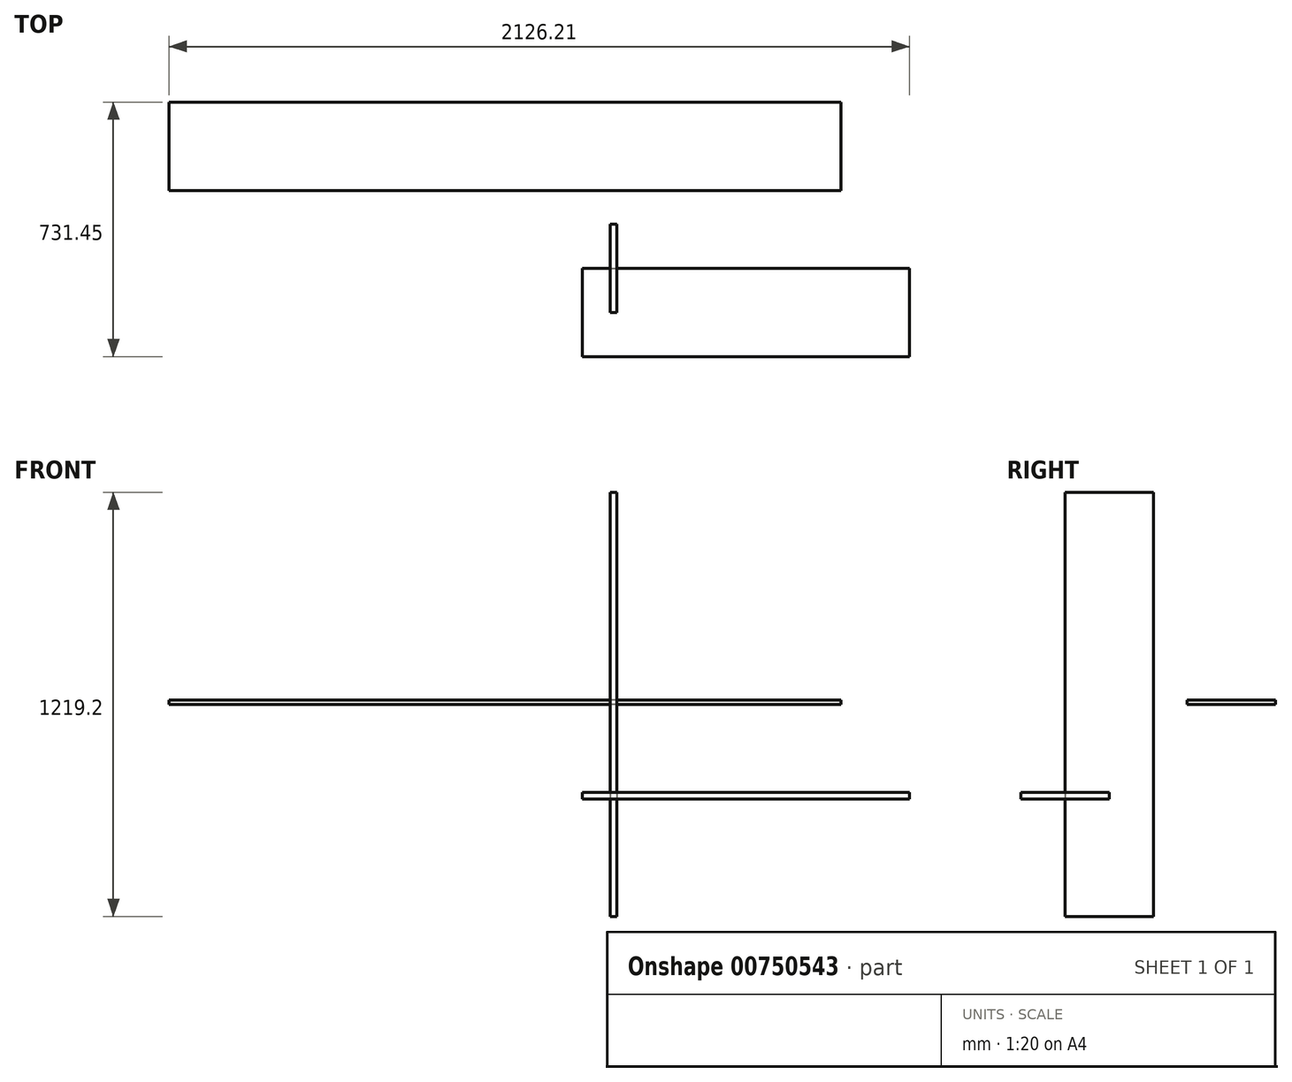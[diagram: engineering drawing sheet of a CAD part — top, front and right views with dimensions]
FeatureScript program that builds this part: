
annotation { "Feature Type Name" : "Feature", "Feature Type Description" : "" }
export const myFeature = defineFeature(function(context is Context, id is Id, definition is map)
    precondition{}
    {
        {
            var Q0;
            Q0=qCreatedBy(makeId("Right.planeOp"),FACE);
            var sketch = newSketch(context, id + "F0", { "sketchPlane" : qUnion([Q0])});
            skLineSegment(sketch, "E0.bottom", {"start": v(-127, 609.6) * mm, "end": v(127, 609.6) * mm});
            skLineSegment(sketch, "E0.top", {"start": v(-127, -609.6) * mm, "end": v(127, -609.6) * mm});
            skLineSegment(sketch, "E0.left", {"start": v(-127, 609.6) * mm, "end": v(-127, -609.6) * mm});
            skLineSegment(sketch, "E0.right", {"start": v(127, 609.6) * mm, "end": v(127, -609.6) * mm});
            skPoint(sketch, "E0.middle", {"position": v(0, 0) * mm});
            skSolve(sketch);
        }
        {
            var Q0;
            Q0=makeQuery(id+"F0.imprint","IMPRINT",FACE,{"disambiguationData":[TD([[makeQuery(id+"F0.imprint","IMPRINT",EDGE,{"derivedFrom":sQuery(id+"F0.wireOp",EDGE,"E0.bottom")}),-1.0]])]});
            extrude(context, id + "F1", {"entities" : qUnion([Q0]), "depth" : 19.05 * mm, "offsetDistance" : 25.4 * mm});
        }
        {
            var Q0;
            Q0=qCreatedBy(makeId("Top.planeOp"),FACE);
            var sketch = newSketch(context, id + "F2", { "sketchPlane" : qUnion([Q0])});
            skLineSegment(sketch, "E1.bottom", {"start": v(662.95, 223.45) * mm, "end": v(-1267.45, 223.45) * mm});
            skLineSegment(sketch, "E1.top", {"start": v(662.95, 477.45) * mm, "end": v(-1267.45, 477.45) * mm});
            skLineSegment(sketch, "E1.left", {"start": v(662.95, 223.45) * mm, "end": v(662.95, 477.45) * mm});
            skLineSegment(sketch, "E1.right", {"start": v(-1267.45, 223.45) * mm, "end": v(-1267.45, 477.45) * mm});
            skSolve(sketch);
        }
        {
            var Q0;
            Q0 = qSketchRegion(id + "F2", true);
            extrude(context, id + "F3", {"entities" : qUnion([Q0]), "depth" : 12.7 * mm, "offsetDistance" : 25.4 * mm});
        }
        {
            var Q0;
            Q0=qCreatedBy(makeId("Front.planeOp"),FACE);
            var sketch = newSketch(context, id + "F4", { "sketchPlane" : qUnion([Q0])});
            skLineSegment(sketch, "E2.bottom", {"start": v(-81.04, -253.37) * mm, "end": v(858.76, -253.37) * mm});
            skLineSegment(sketch, "E2.top", {"start": v(-81.04, -272.42) * mm, "end": v(858.76, -272.42) * mm});
            skLineSegment(sketch, "E2.left", {"start": v(-81.04, -253.37) * mm, "end": v(-81.04, -272.42) * mm});
            skLineSegment(sketch, "E2.right", {"start": v(858.76, -253.37) * mm, "end": v(858.76, -272.42) * mm});
            skSolve(sketch);
        }
        {
            var Q0;
            Q0 = qSketchRegion(id + "F4", true);
            extrude(context, id + "F5", {"entities" : qUnion([Q0]), "depth" : 254 * mm, "offsetDistance" : 25.4 * mm});
        }
    });
